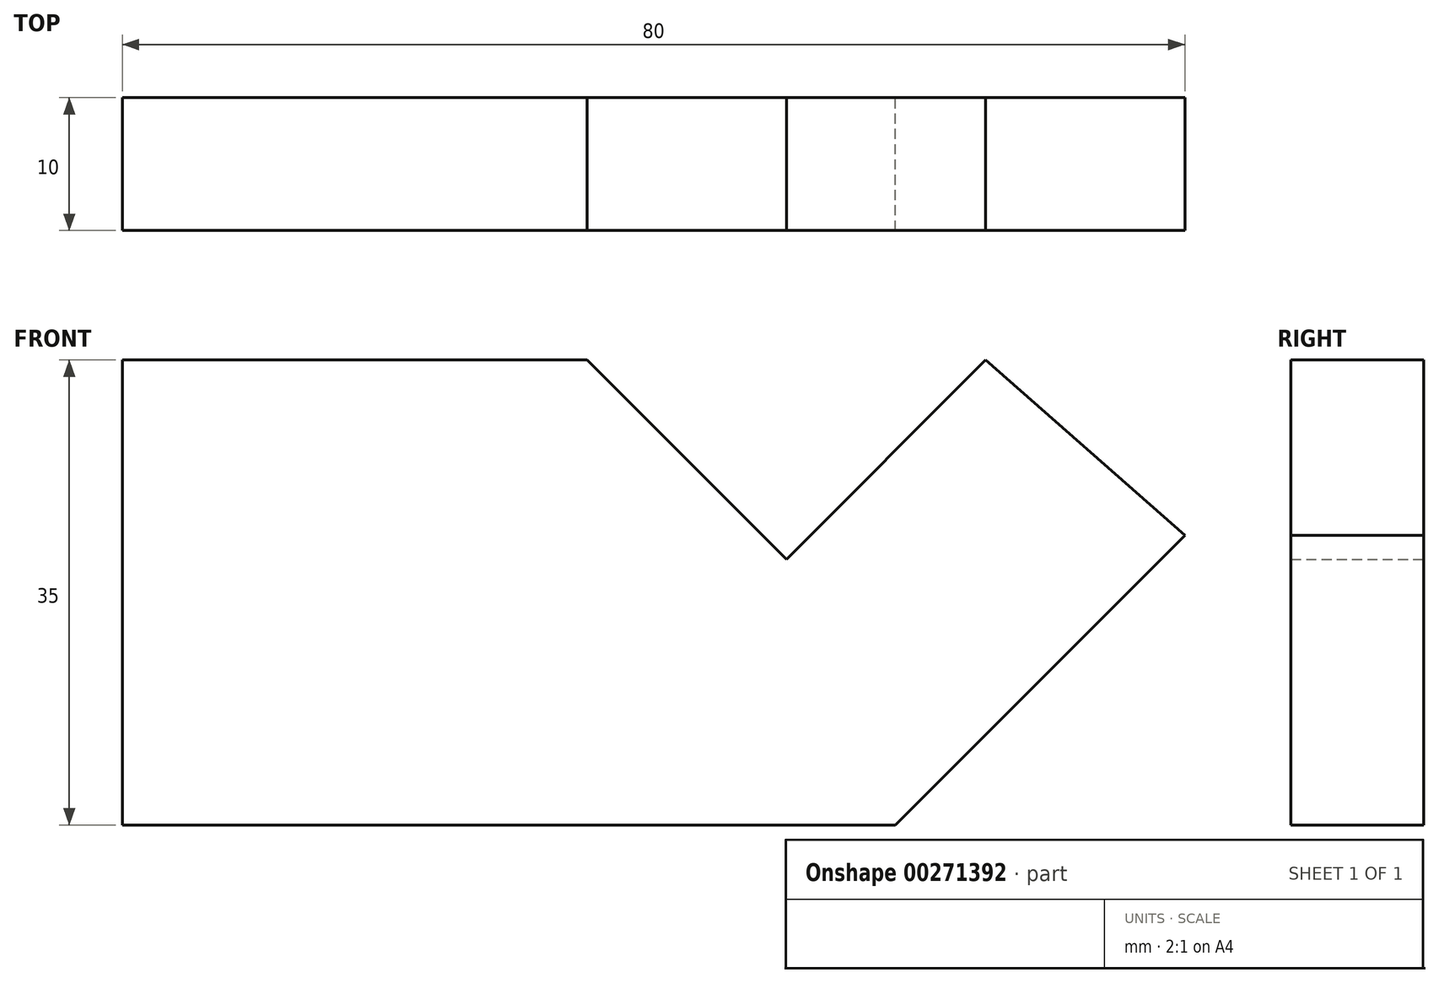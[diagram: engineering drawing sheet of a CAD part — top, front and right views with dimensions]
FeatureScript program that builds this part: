
annotation { "Feature Type Name" : "Feature", "Feature Type Description" : "" }
export const myFeature = defineFeature(function(context is Context, id is Id, definition is map)
    precondition{}
    {
        {
            var Q0;
            Q0=qCreatedBy(makeId("Front.planeOp"),FACE);
            var sketch = newSketch(context, id + "F0", { "sketchPlane" : qUnion([Q0])});
            skLineSegment(sketch, "E0", {"start": v(0, 0) * mm, "end": v(58.2, 0) * mm});
            skLineSegment(sketch, "E1", {"start": v(0, 35) * mm, "end": v(0, 0) * mm});
            skLineSegment(sketch, "E2", {"start": v(0, 35) * mm, "end": v(35, 35) * mm});
            skLineSegment(sketch, "E3", {"start": v(35, 35) * mm, "end": v(50, 20) * mm});
            skLineSegment(sketch, "E4", {"start": v(50, 20) * mm, "end": v(65, 35) * mm});
            skLineSegment(sketch, "E5", {"start": v(65, 35) * mm, "end": v(80, 21.8) * mm});
            skLineSegment(sketch, "E6", {"start": v(80, 21.8) * mm, "end": v(58.2, 0) * mm});
            skSolve(sketch);
        }
        {
            var Q0;
            Q0 = qSketchRegion(id + "F0", true);
            extrude(context, id + "F1", {"entities" : qUnion([Q0]), "depth" : 10 * mm});
        }
    });
